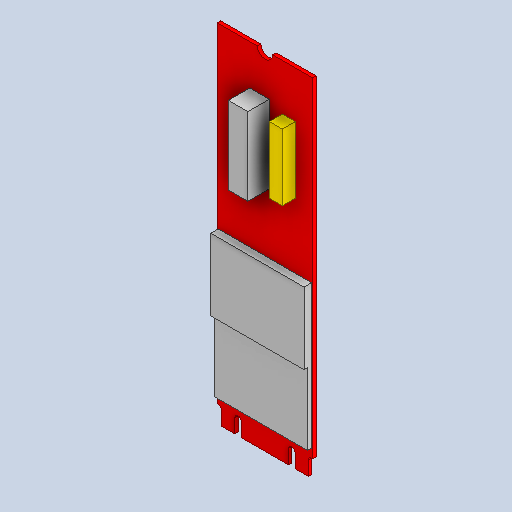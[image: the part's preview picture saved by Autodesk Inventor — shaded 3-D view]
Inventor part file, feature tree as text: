
AUTODESK INVENTOR PART (.ipt)
format: ipt  version: 2024.2 (Build 282272000, 272)  size: 407,552 bytes
history: native  units: mm
features: extrude x10, sketch x10, projected_geometry x4, fillet x1
ambient origin geometry x8: Origin, YZ Plane, XZ Plane, XY Plane, X Axis, Y Axis, Z Axis, Center Point
bodies: Solid1 (feature_tree), Solid2 (feature_tree), Solid3 (feature_tree), Solid5 (feature_tree), Solid6 (feature_tree), Solid7 (feature_tree)
feature tree (25):
  extrude  "Extrusion1"  Depth=80.0mm
  extrude  "Extrusion2"  Depth=1.0mm
  fillet  "Fillet1"  Radius=1.0mm
  extrude  "Extrusion3"  Depth=1.5mm
  extrude  "Extrusion4"  Depth=0.75mm
  extrude  "Extrusion5"  Depth=40.0mm
  extrude  "Extrusion6"  Depth=1.5mm
  extrude  "Extrusion7"  Depth=45.0mm
  extrude  "Extrusion8"  Depth=5.0mm TaperAngle=0.0deg
  extrude  "Extrusion9"  Depth=12.4mm TaperAngle=0.0deg
  extrude  "Extrusion10"  Depth=15.3mm
  sketch  "Sketch1"  dims[d0=22.0mm d1=80.0mm]
  sketch  "Sketch2"  dims[d2=0.8mm d3=0.0mm d4=1.0mm d5=1.0mm]
  projected_geometry  "Projected Loop1"
  sketch  "Sketch3"  dims[d6=4.0mm d7=1.5mm]
  projected_geometry  "Projected Loop2"
  sketch  "Sketch4"  dims[d9=0.8mm d10=0.0mm d11=0.75mm]
  sketch  "Sketch5"  dims[d12=5.2mm d13=40.0mm]
  projected_geometry  "Projected Loop3"
  sketch  "Sketch6"  dims[d14=11.6mm d15=0.0mm d16=1.5mm]
  sketch  "Sketch7"  dims[d17=1.5mm d18=45.0mm]
  sketch  "Sketch8"  dims[d19=2.2mm d20=0.0mm d21=5.0mm d22=0.0mm]
  sketch  "Sketch9"  dims[d23=3.5mm d24=12.4mm d25=0.0mm]
  sketch  "Sketch10"  dims[d26=3.0mm d27=15.3mm d28=10.7mm d29=4.0mm d30=3.0mm d31=0.0mm d32=4.5mm d36=3.0mm d37=4.93mm d38=0.0mm d39=4.825mm d40=33.0mm d42=6.0mm d43=0.25mm d44=0.25mm d45=1.73mm d46=0.0mm d47=9.25mm d48=17.9mm d49=0.8mm d50=0.0mm]
  projected_geometry  "Projected Loop4"
